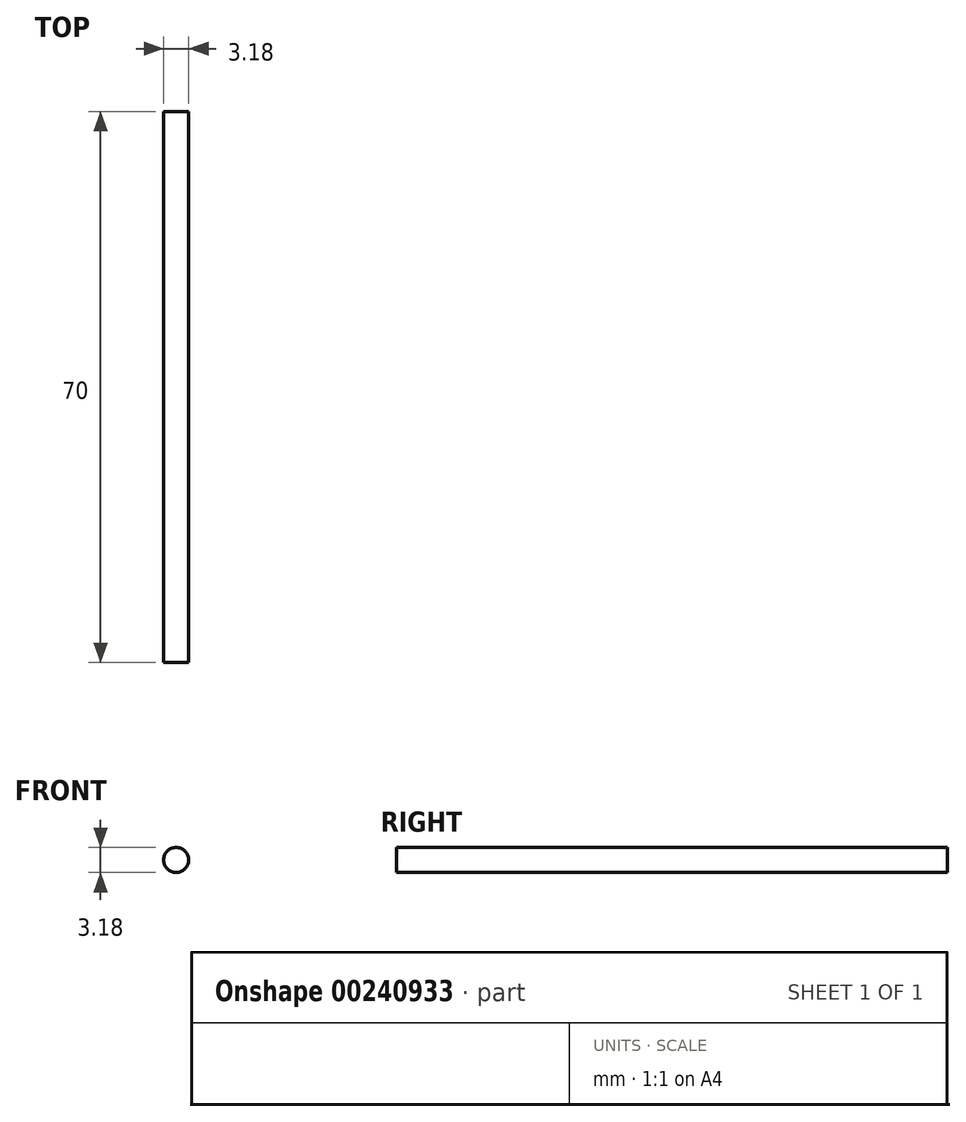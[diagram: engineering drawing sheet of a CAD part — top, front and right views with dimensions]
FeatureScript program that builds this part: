
annotation { "Feature Type Name" : "Feature", "Feature Type Description" : "" }
export const myFeature = defineFeature(function(context is Context, id is Id, definition is map)
    precondition{}
    {
        {
            var Q0;
            Q0=qCreatedBy(makeId("Front.planeOp"),FACE);
            var sketch = newSketch(context, id + "F0", { "sketchPlane" : qUnion([Q0])});
            skCircle(sketch, "E0", {"center": v(0, 0) * mm, "radius": 1.59 * mm});
            skSolve(sketch);
        }
        {
            var Q0;
            Q0=qSketchRegion(id+"F0",true);
            extrude(context, id + "F1", {"entities" : qUnion([Q0]), "depth" : 70 * mm});
        }
    });
